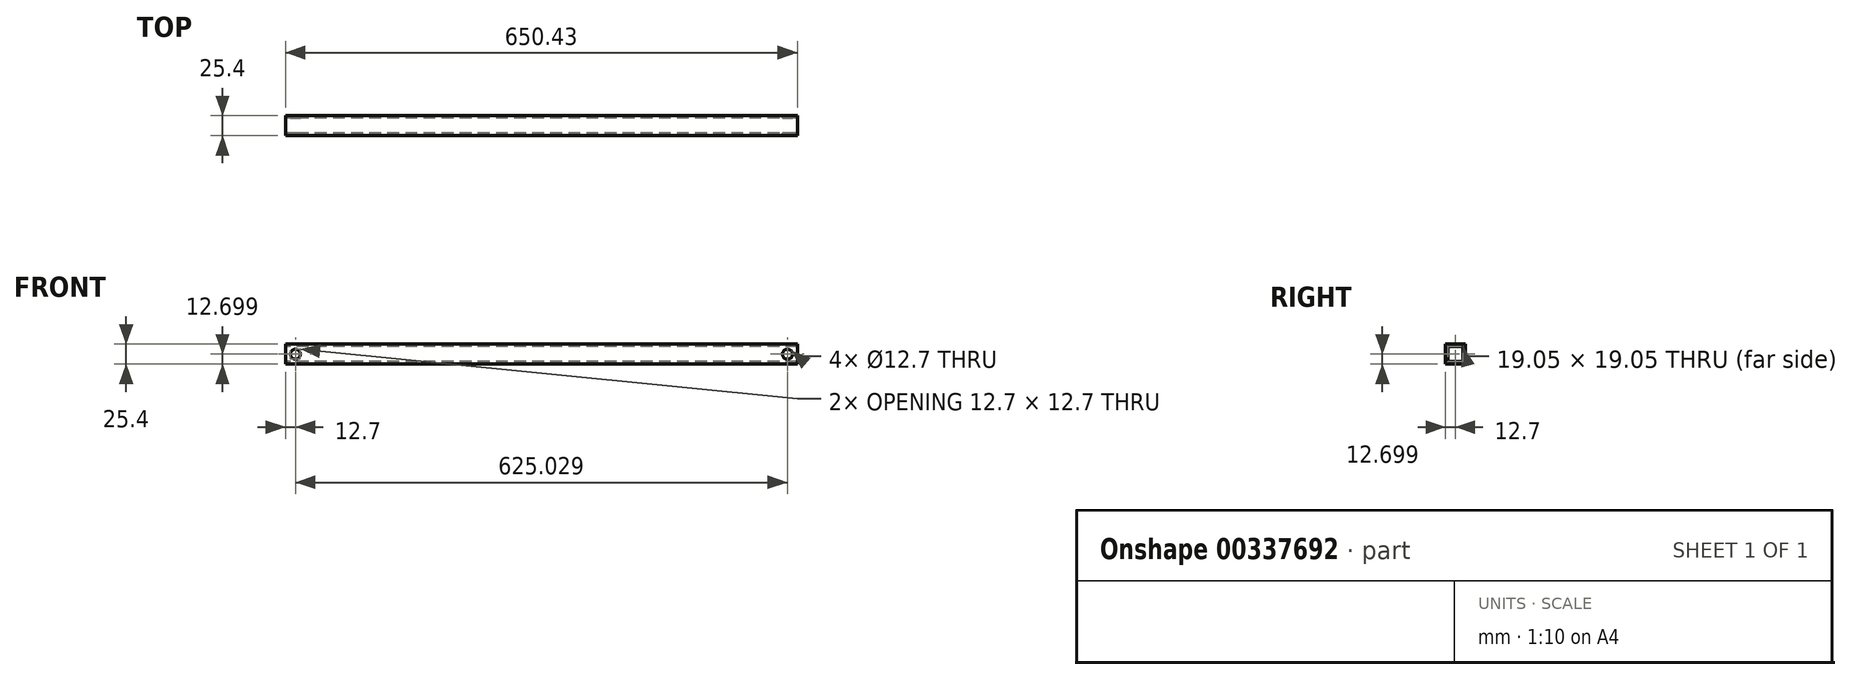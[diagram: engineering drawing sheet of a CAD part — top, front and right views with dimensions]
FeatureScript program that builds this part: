
annotation { "Feature Type Name" : "Feature", "Feature Type Description" : "" }
export const myFeature = defineFeature(function(context is Context, id is Id, definition is map)
    precondition{}
    {
        {
            var Q0;
            Q0=qCreatedBy(makeId("Front.planeOp"),FACE);
            var sketch = newSketch(context, id + "F0", { "sketchPlane" : qUnion([Q0])});
            skLineSegment(sketch, "E0.bottom", {"start": v(-306.95, -9.17) * mm, "end": v(318.08, -9.17) * mm});
            skLineSegment(sketch, "E0.top", {"start": v(-306.95, -34.57) * mm, "end": v(318.08, -34.57) * mm});
            skLineSegment(sketch, "E0.left", {"start": v(-306.95, -9.17) * mm, "end": v(-306.95, -34.57) * mm});
            skLineSegment(sketch, "E0.right", {"start": v(318.08, -9.17) * mm, "end": v(318.08, -34.57) * mm});
            skArc(sketch, "E1", {"start": v(-306.95, -9.17) * mm, "mid": v(-319.65, -21.87) * mm, "end": v(-306.95, -34.57) * mm});
            skArc(sketch, "E2", {"start": v(318.08, -34.57) * mm, "mid": v(330.78, -21.87) * mm, "end": v(318.08, -9.17) * mm});
            skCircle(sketch, "E3", {"center": v(-306.95, -21.87) * mm, "radius": 6.35 * mm});
            skCircle(sketch, "E4", {"center": v(318.08, -21.87) * mm, "radius": 6.35 * mm});
            skPoint(sketch, "E5.oppositeSnap0", {"position": v(330.78, -21.87) * mm});
            skLineSegment(sketch, "E5.bottom", {"start": v(318.08, -9.17) * mm, "end": v(330.78, -9.17) * mm});
            skLineSegment(sketch, "E5.top", {"start": v(318.08, -34.57) * mm, "end": v(330.78, -34.57) * mm});
            skLineSegment(sketch, "E5.right", {"start": v(330.78, -9.17) * mm, "end": v(330.78, -34.57) * mm});
            skPoint(sketch, "E6.oppositeSnap0", {"position": v(-319.65, -21.87) * mm});
            skLineSegment(sketch, "E6.bottom", {"start": v(-306.95, -9.17) * mm, "end": v(-319.65, -9.17) * mm});
            skLineSegment(sketch, "E6.top", {"start": v(-306.95, -34.57) * mm, "end": v(-319.65, -34.57) * mm});
            skLineSegment(sketch, "E6.right", {"start": v(-319.65, -9.17) * mm, "end": v(-319.65, -34.57) * mm});
            skSolve(sketch);
        }
        {
            var Q0;
            {var subQ5=sQuery(id+"F0.wireOp",EDGE,"E0.bottom");Q0=makeQuery(id+"F0.imprint","IMPRINT",FACE,{"disambiguationData":[TD([[makeQuery(id+"F0.imprint","IMPRINT",EDGE,{"derivedFrom":subQ5}),-1.0]])]});}
            var Q1;
            {var subQ0=sQuery(id+"F0.wireOp",EDGE,"E1");Q1=makeQuery(id+"F0.imprint","IMPRINT",FACE,{"disambiguationData":[TD([[makeQuery(id+"F0.imprint","IMPRINT",EDGE,{"derivedFrom":subQ0}),1.0]])]});}
            var Q2;
            {var subQ0=sQuery(id+"F0.wireOp",EDGE,"E5.bottom");Q2=makeQuery(id+"F0.imprint","IMPRINT",FACE,{"disambiguationData":[TD([[makeQuery(id+"F0.imprint","IMPRINT",EDGE,{"derivedFrom":subQ0}),-1.0]])]});}
            var Q3;
            {var subQ0=sQuery(id+"F0.wireOp",EDGE,"E5.top");Q3=makeQuery(id+"F0.imprint","IMPRINT",FACE,{"disambiguationData":[TD([[makeQuery(id+"F0.imprint","IMPRINT",EDGE,{"derivedFrom":subQ0}),1.0]])]});}
            var Q4;
            {var subQ0=sQuery(id+"F0.wireOp",EDGE,"E0.right");var subQ3=sQuery(id+"F0.wireOp",EDGE,"E4");var subQ4=makeQuery(id+"F0.imprint","INTERSECT",VERTEX,{"disambiguationData":[OD(0.0)],"derivedFrom":[subQ3,subQ0]});Q4=makeQuery(id+"F0.imprint","IMPRINT",FACE,{"disambiguationData":[TD([[makeQuery(id+"F0.imprint","IMPRINT",EDGE,{"disambiguationData":[TD([[subQ4,1.0]])],"derivedFrom":subQ3}),-1.0]])]});}
            var Q5;
            {var subQ0=sQuery(id+"F0.wireOp",EDGE,"E6.bottom");Q5=makeQuery(id+"F0.imprint","IMPRINT",FACE,{"disambiguationData":[TD([[makeQuery(id+"F0.imprint","IMPRINT",EDGE,{"derivedFrom":subQ0}),1.0]])]});}
            var Q6;
            {var subQ0=sQuery(id+"F0.wireOp",EDGE,"E6.top");Q6=makeQuery(id+"F0.imprint","IMPRINT",FACE,{"disambiguationData":[TD([[makeQuery(id+"F0.imprint","IMPRINT",EDGE,{"derivedFrom":subQ0}),-1.0]])]});}
            extrude(context, id + "F1", {"entities" : qUnion([Q0, Q1, Q2, Q3, Q4, Q5, Q6]), "depth" : 25.4 * mm});
        }
        {
            var Q0;
            Q0=makeQuery(id+"F1.opExtrude","SWEPT_FACE",FACE,{"disambiguationData":[OSD([sQuery(id+"F0.wireOp",EDGE,"E6.right")])]});
            var sketch = newSketch(context, id + "F2", { "sketchPlane" : qUnion([Q0])});
            skLineSegment(sketch, "E7.bottom", {"start": v(3.17, -12.35) * mm, "end": v(22.23, -12.35) * mm});
            skLineSegment(sketch, "E7.top", {"start": v(3.18, -31.4) * mm, "end": v(22.23, -31.4) * mm});
            skLineSegment(sketch, "E7.left", {"start": v(3.17, -12.35) * mm, "end": v(3.18, -31.4) * mm});
            skLineSegment(sketch, "E7.right", {"start": v(22.23, -12.35) * mm, "end": v(22.23, -31.4) * mm});
            skSolve(sketch);
        }
        {
            var Q0;
            Q0 = qSketchRegion(id + "F2", true);
            extrude(context, id + "F3", {"entities" : qUnion([Q0]), "operationType" : NewBodyOperationType.REMOVE, "endBound" : BoundingType.THROUGH_ALL, "oppositeDirection" : true, "depth" : 25.4 * mm});
        }
    });
